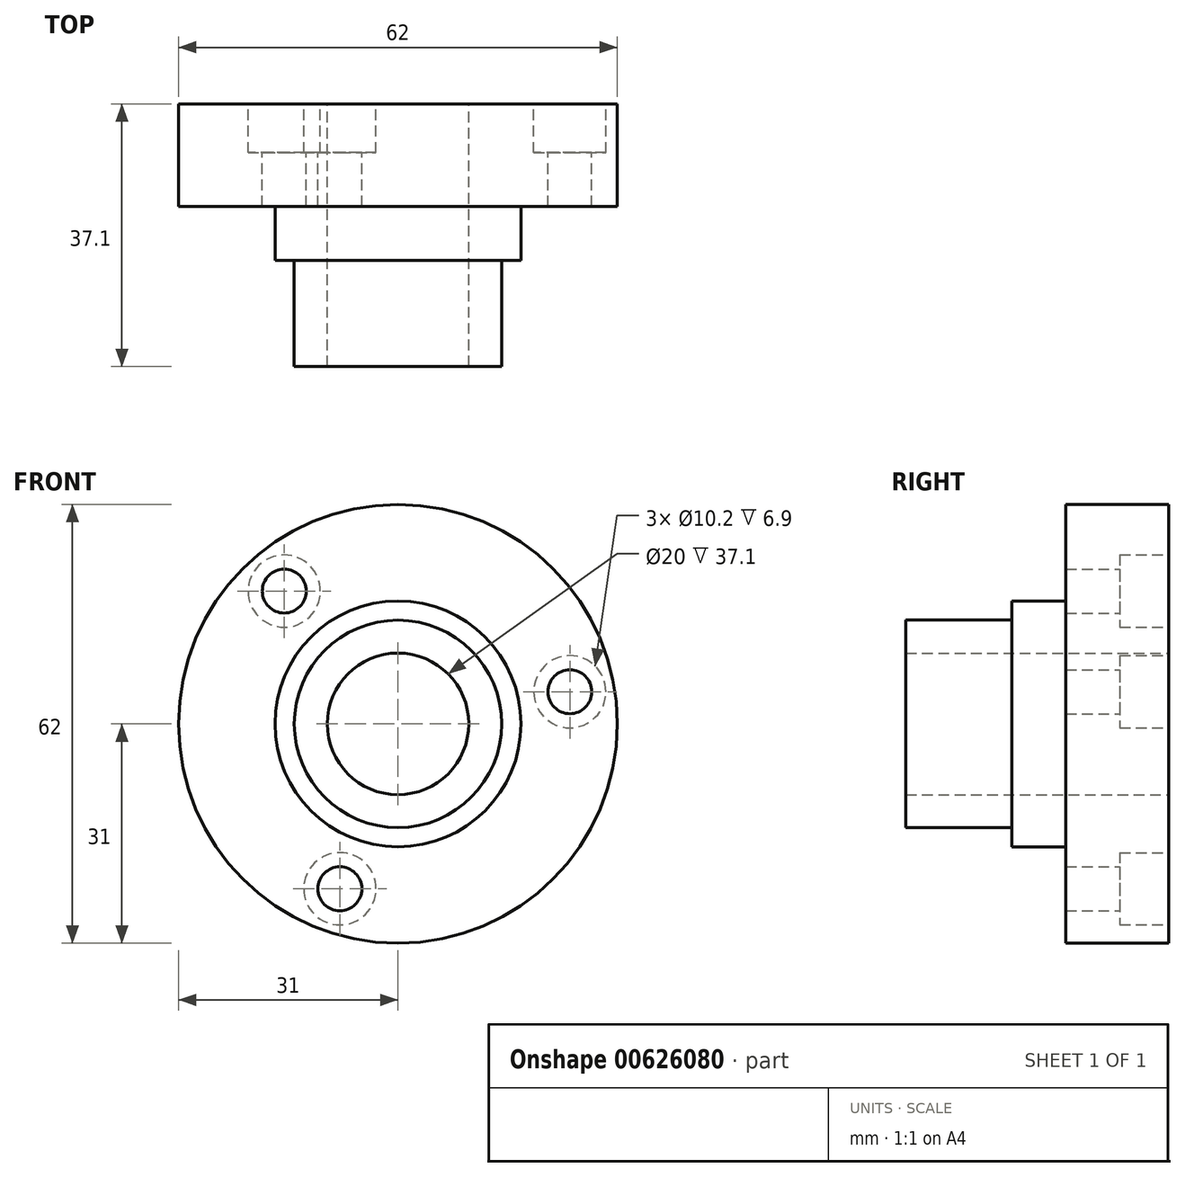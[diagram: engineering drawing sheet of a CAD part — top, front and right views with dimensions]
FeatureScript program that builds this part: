
annotation { "Feature Type Name" : "Feature", "Feature Type Description" : "" }
export const myFeature = defineFeature(function(context is Context, id is Id, definition is map)
    precondition{}
    {
        {
            var Q0;
            Q0=qCreatedBy(makeId("Right.planeOp"),FACE);
            var sketch = newSketch(context, id + "F0", { "sketchPlane" : qUnion([Q0])});
            skLineSegment(sketch, "E0", {"start": v(-37.1, 14.65) * mm, "end": v(-22.1, 14.65) * mm});
            skLineSegment(sketch, "E1", {"start": v(-22.1, 14.65) * mm, "end": v(-22.1, 17.38) * mm});
            skLineSegment(sketch, "E2", {"start": v(-22.1, 17.38) * mm, "end": v(-14.5, 17.38) * mm});
            skLineSegment(sketch, "E3", {"start": v(-14.5, 17.38) * mm, "end": v(-14.5, 31) * mm});
            skLineSegment(sketch, "E4", {"start": v(-14.5, 31) * mm, "end": v(0, 31) * mm});
            skLineSegment(sketch, "E5", {"start": v(0, 31) * mm, "end": v(0, 0) * mm});
            skLineSegment(sketch, "E6", {"start": v(0, 0) * mm, "end": v(-37.1, 0) * mm});
            skLineSegment(sketch, "E7", {"start": v(-37.1, 0) * mm, "end": v(-37.1, 14.65) * mm});
            skSolve(sketch);
        }
        {
            var Q0;
            Q0=makeQuery(id+"F0.imprint","IMPRINT",FACE,{"disambiguationData":[TD([[makeQuery(id+"F0.imprint","IMPRINT",EDGE,{"derivedFrom":sQuery(id+"F0.wireOp",EDGE,"E0")}),-1.0]])]});
            var Q1;
            Q1=sQuery(id+"F0.wireOp",EDGE,"E6");
            revolve(context, id + "F1", {"entities" : qUnion([Q0]), "axis" : qUnion([Q1]), "revolveType" : RevolveType.FULL});
        }
        {
            var Q0;
            Q0=makeQuery(id+"F1.opRevolve","SWEPT_FACE",FACE,{"disambiguationData":[OSD([sQuery(id+"F0.wireOp",EDGE,"E5")])]});
            var sketch = newSketch(context, id + "F2", { "sketchPlane" : qUnion([Q0])});
            skCircle(sketch, "E8", {"center": v(0, 0) * mm, "radius": 10 * mm});
            skCircle(sketch, "E9", {"center": v(16.07, 18.76) * mm, "radius": 5.1 * mm});
            skCircle(sketch, "E10", {"center": v(16.07, 18.76) * mm, "radius": 3.1 * mm});
            skCircle(sketch, "E11.1.0", {"center": v(-24.28, 4.54) * mm, "radius": 3.1 * mm});
            skCircle(sketch, "E11.1.1", {"center": v(-24.28, 4.54) * mm, "radius": 5.1 * mm});
            skCircle(sketch, "E11.2.0", {"center": v(8.2, -23.3) * mm, "radius": 3.1 * mm});
            skCircle(sketch, "E11.2.1", {"center": v(8.2, -23.3) * mm, "radius": 5.1 * mm});
            skSolve(sketch);
        }
        {
            var Q0;
            Q0=makeQuery(id+"F2.imprint","IMPRINT",FACE,{"disambiguationData":[TD([[makeQuery(id+"F2.imprint","IMPRINT",EDGE,{"derivedFrom":sQuery(id+"F2.wireOp",EDGE,"E11.1.0")}),1.0]])]});
            var Q1;
            Q1=makeQuery(id+"F2.imprint","IMPRINT",FACE,{"disambiguationData":[TD([[makeQuery(id+"F2.imprint","IMPRINT",EDGE,{"derivedFrom":sQuery(id+"F2.wireOp",EDGE,"E8")}),1.0]])]});
            var Q2;
            Q2=makeQuery(id+"F2.imprint","IMPRINT",FACE,{"disambiguationData":[TD([[makeQuery(id+"F2.imprint","IMPRINT",EDGE,{"derivedFrom":sQuery(id+"F2.wireOp",EDGE,"E10")}),1.0]])]});
            var Q3;
            Q3=makeQuery(id+"F2.imprint","IMPRINT",FACE,{"disambiguationData":[TD([[makeQuery(id+"F2.imprint","IMPRINT",EDGE,{"derivedFrom":sQuery(id+"F2.wireOp",EDGE,"E11.2.0")}),1.0]])]});
            extrude(context, id + "F3", {"entities" : qUnion([Q0, Q1, Q2, Q3]), "operationType" : NewBodyOperationType.REMOVE, "oppositeDirection" : true, "depth" : 47.8 * mm, "offsetDistance" : 25 * mm});
        }
        {
            var Q0;
            Q0=makeQuery(id+"F2.imprint","IMPRINT",FACE,{"disambiguationData":[TD([[makeQuery(id+"F2.imprint","IMPRINT",EDGE,{"derivedFrom":sQuery(id+"F2.wireOp",EDGE,"E11.1.0")}),-1.0]])]});
            var Q1;
            Q1=makeQuery(id+"F2.imprint","IMPRINT",FACE,{"disambiguationData":[TD([[makeQuery(id+"F2.imprint","IMPRINT",EDGE,{"derivedFrom":sQuery(id+"F2.wireOp",EDGE,"E9")}),1.0]])]});
            var Q2;
            Q2=makeQuery(id+"F2.imprint","IMPRINT",FACE,{"disambiguationData":[TD([[makeQuery(id+"F2.imprint","IMPRINT",EDGE,{"derivedFrom":sQuery(id+"F2.wireOp",EDGE,"E11.2.0")}),-1.0]])]});
            extrude(context, id + "F4", {"entities" : qUnion([Q0, Q1, Q2]), "operationType" : NewBodyOperationType.REMOVE, "oppositeDirection" : true, "depth" : 6.9 * mm, "offsetDistance" : 25 * mm});
        }
    });
